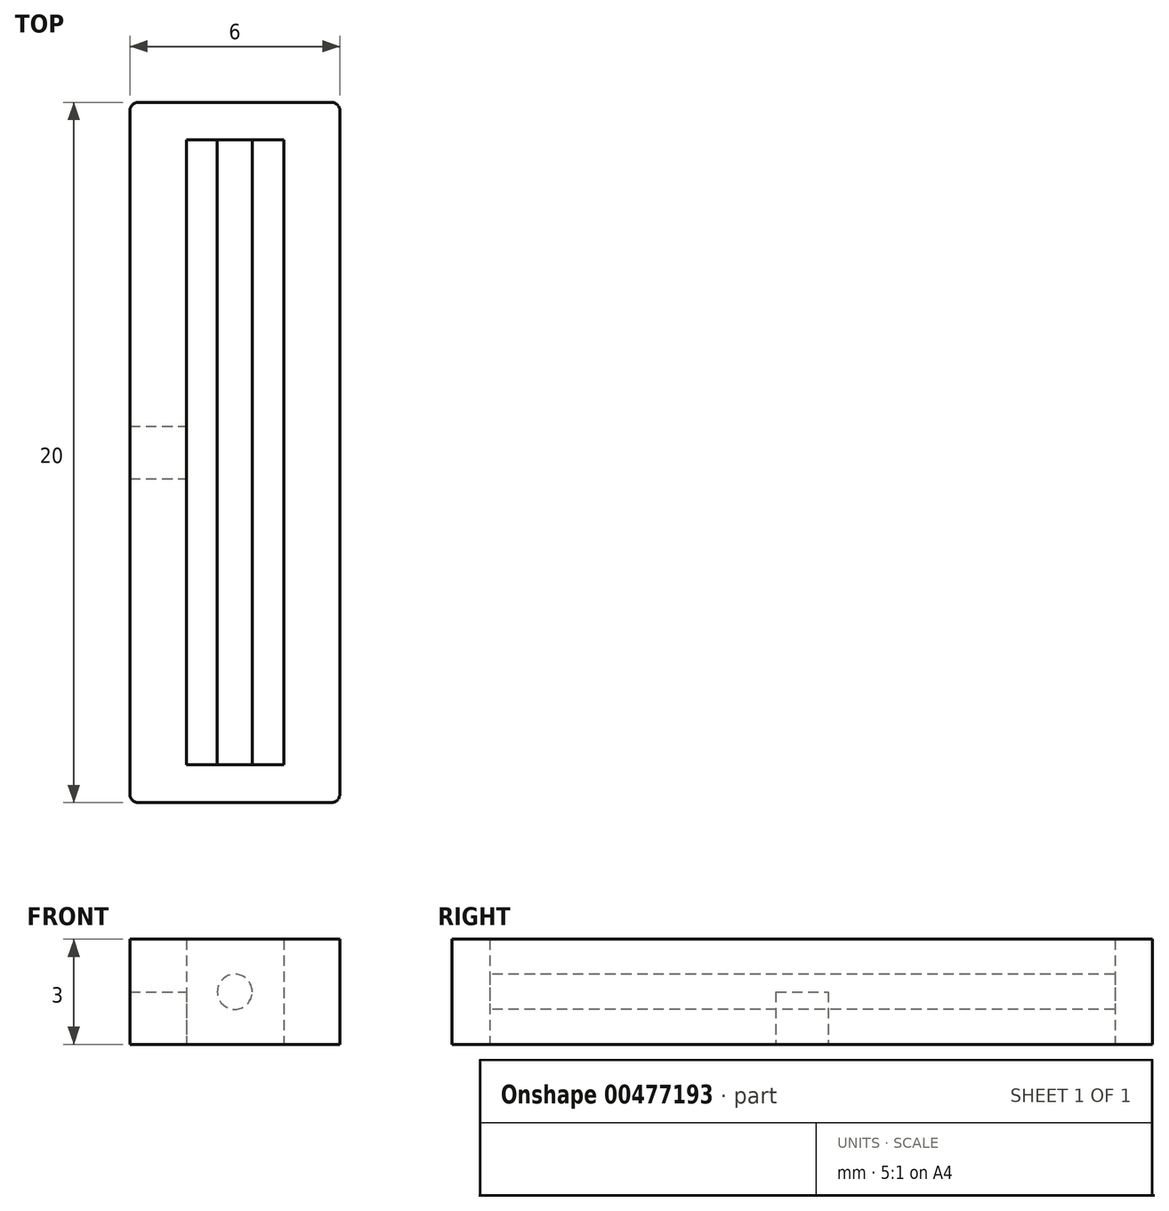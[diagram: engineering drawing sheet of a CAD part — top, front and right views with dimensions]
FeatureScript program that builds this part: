
annotation { "Feature Type Name" : "Feature", "Feature Type Description" : "" }
export const myFeature = defineFeature(function(context is Context, id is Id, definition is map)
    precondition{}
    {
        {
            var Q0;
            Q0=qCreatedBy(makeId("Top.planeOp"),FACE);
            var sketch = newSketch(context, id + "F0", { "sketchPlane" : qUnion([Q0])});
            skLineSegment(sketch, "E0.bottom", {"start": v(-3, 10) * mm, "end": v(3, 10) * mm});
            skLineSegment(sketch, "E0.top", {"start": v(-3, -10) * mm, "end": v(3, -10) * mm});
            skLineSegment(sketch, "E0.left", {"start": v(-3, 10) * mm, "end": v(-3, -10) * mm});
            skLineSegment(sketch, "E0.right", {"start": v(3, 10) * mm, "end": v(3, -10) * mm});
            skPoint(sketch, "E0.middle", {"position": v(0, 0) * mm});
            skSolve(sketch);
        }
        {
            var Q0;
            Q0 = qSketchRegion(id + "F0", true);
            extrude(context, id + "F1", {"entities" : qUnion([Q0]), "depth" : 3 * mm});
        }
        {
            var Q0;
            Q0=makeQuery(id+"F1.opExtrude","SWEPT_EDGE",EDGE,{"disambiguationData":[OSD([sQuery(id+"F0.wireOp",EDGE,"E0.bottom"),sQuery(id+"F0.wireOp",EDGE,"E0.right")])]});
            var Q1;
            Q1=makeQuery(id+"F1.opExtrude","SWEPT_EDGE",EDGE,{"disambiguationData":[OSD([sQuery(id+"F0.wireOp",EDGE,"E0.bottom"),sQuery(id+"F0.wireOp",EDGE,"E0.left")])]});
            var Q2;
            Q2=makeQuery(id+"F1.opExtrude","SWEPT_EDGE",EDGE,{"disambiguationData":[OSD([sQuery(id+"F0.wireOp",EDGE,"E0.top"),sQuery(id+"F0.wireOp",EDGE,"E0.left")])]});
            var Q3;
            Q3=makeQuery(id+"F1.opExtrude","SWEPT_EDGE",EDGE,{"disambiguationData":[OSD([sQuery(id+"F0.wireOp",EDGE,"E0.top"),sQuery(id+"F0.wireOp",EDGE,"E0.right")])]});
            fillet(context, id + "F2", {"entities" : qUnion([Q0, Q1, Q2, Q3]), "radius" : 0.25 * mm, "tangentPropagation" : true, "allowEdgeOverflow" : false});
        }
        {
            var Q0;
            Q0=qCreatedBy(makeId("Top.planeOp"),FACE);
            var sketch = newSketch(context, id + "F3", { "sketchPlane" : qUnion([Q0])});
            skLineSegment(sketch, "E1.bottom", {"start": v(-1.38, 8.93) * mm, "end": v(1.4, 8.93) * mm});
            skLineSegment(sketch, "E1.top", {"start": v(-1.38, -8.91) * mm, "end": v(1.4, -8.91) * mm});
            skLineSegment(sketch, "E1.left", {"start": v(-1.38, 8.93) * mm, "end": v(-1.38, -8.91) * mm});
            skLineSegment(sketch, "E1.right", {"start": v(1.4, 8.93) * mm, "end": v(1.4, -8.91) * mm});
            skSolve(sketch);
        }
        {
            var Q0;
            Q0 = qSketchRegion(id + "F3", true);
            extrude(context, id + "F4", {"entities" : qUnion([Q0]), "operationType" : NewBodyOperationType.REMOVE, "depth" : 5.9 * mm});
        }
        {
            var Q0;
            Q0=makeQuery(id+"F1.opExtrude","SWEPT_FACE",FACE,{"disambiguationData":[OSD([sQuery(id+"F0.wireOp",EDGE,"E0.top")])]});
            cPlane(context, id + "F5", {"entities" : qUnion([Q0]), "cplaneType" : CPlaneType.OFFSET, "offset" : 0 * mm, "width" : 150 * mm, "height" : 150 * mm});
        }
        {
            var Q0;
            Q0=qCreatedBy(id+"F5.planeOp",FACE);
            var sketch = newSketch(context, id + "F6", { "sketchPlane" : qUnion([Q0])});
            skCircle(sketch, "E2", {"center": v(0, 1.5) * mm, "radius": 0.5 * mm});
            skSolve(sketch);
        }
        {
            var Q0;
            Q0 = qSketchRegion(id + "F6", true);
            extrude(context, id + "F7", {"entities" : qUnion([Q0]), "operationType" : NewBodyOperationType.ADD, "oppositeDirection" : true, "depth" : 19.2 * mm});
        }
        {
            var Q0;
            Q0=makeQuery(id+"F4.boolean.opBoolean","COPY",FACE,{"derivedFrom":makeQuery(id+"F4.opExtrude","SWEPT_FACE",FACE,{"disambiguationData":[OSD([sQuery(id+"F3.wireOp",EDGE,"E1.left")])]})});
            var sketch = newSketch(context, id + "F8", { "sketchPlane" : qUnion([Q0])});
            skLineSegment(sketch, "E3.bottom", {"start": v(-0.75, 1.5) * mm, "end": v(0.75, 1.5) * mm});
            skLineSegment(sketch, "E3.top", {"start": v(-0.75, -1.5) * mm, "end": v(0.75, -1.5) * mm});
            skLineSegment(sketch, "E3.left", {"start": v(-0.75, 1.5) * mm, "end": v(-0.75, -1.5) * mm});
            skLineSegment(sketch, "E3.right", {"start": v(0.75, 1.5) * mm, "end": v(0.75, -1.5) * mm});
            skPoint(sketch, "E3.middle", {"position": v(0, 0) * mm});
            skSolve(sketch);
        }
        {
            var Q0;
            Q0 = qSketchRegion(id + "F8", true);
            extrude(context, id + "F9", {"entities" : qUnion([Q0]), "operationType" : NewBodyOperationType.REMOVE, "oppositeDirection" : true, "depth" : 3.6 * mm});
        }
    });
